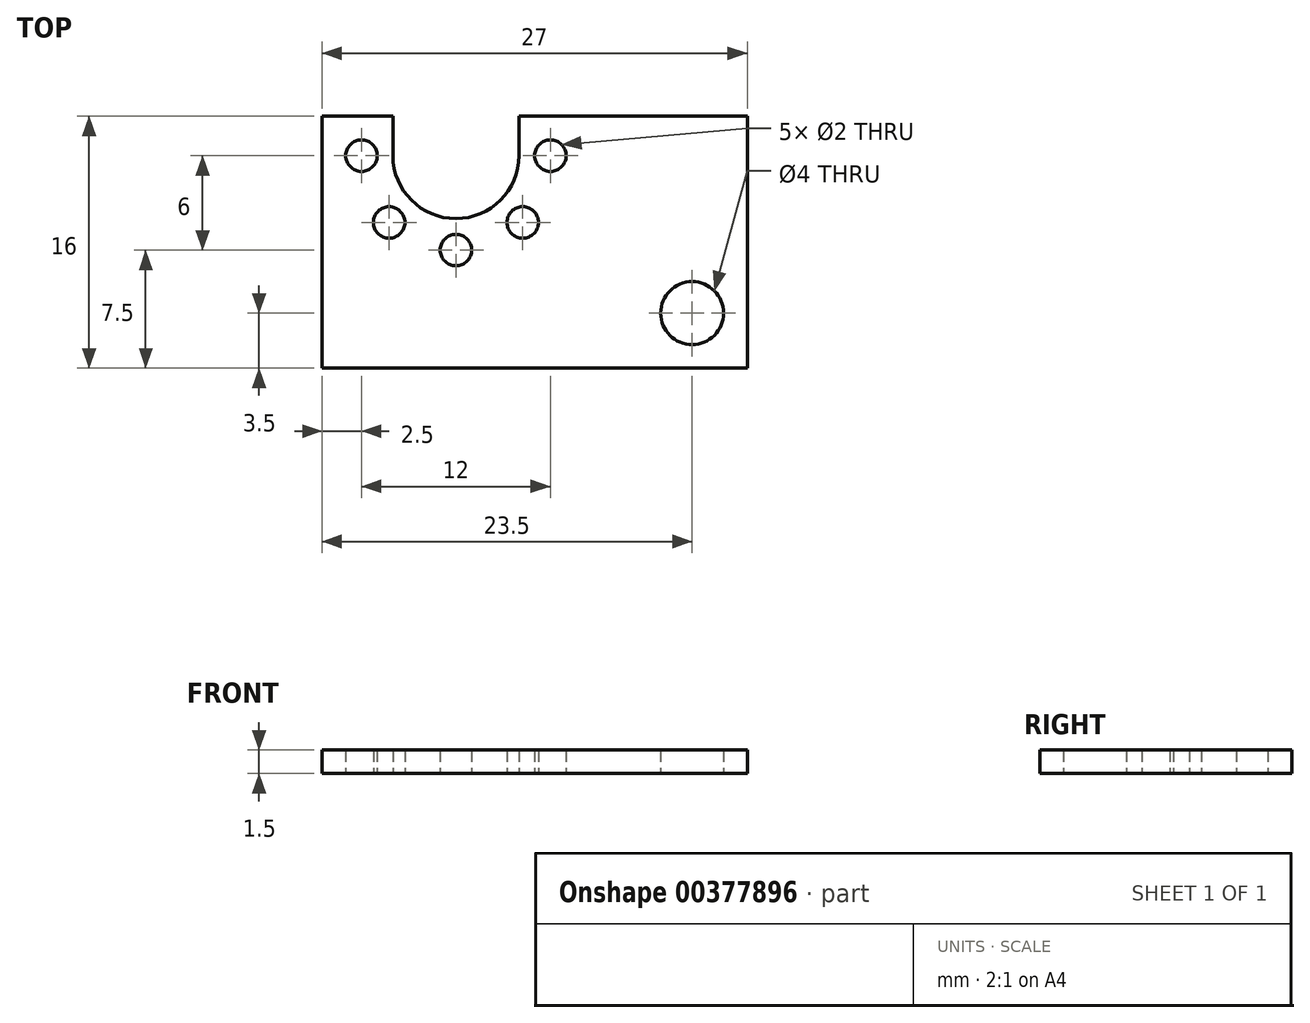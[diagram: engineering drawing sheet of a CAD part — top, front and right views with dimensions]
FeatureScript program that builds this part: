
annotation { "Feature Type Name" : "Feature", "Feature Type Description" : "" }
export const myFeature = defineFeature(function(context is Context, id is Id, definition is map)
    precondition{}
    {
        {
            var Q0;
            Q0=qCreatedBy(makeId("Top.planeOp"),FACE);
            var sketch = newSketch(context, id + "F0", { "sketchPlane" : qUnion([Q0])});
            skArc(sketch, "E0", {"start": v(-4, 0) * mm, "mid": v(0, -4) * mm, "end": v(4, 0) * mm});
            skCircle(sketch, "E1", {"center": v(6, 0) * mm, "radius": 1 * mm});
            skCircle(sketch, "E2.4.0", {"center": v(-6, 0) * mm, "radius": 1 * mm});
            skCircle(sketch, "E2.5.0", {"center": v(-4.24, -4.24) * mm, "radius": 1 * mm});
            skCircle(sketch, "E2.6.0", {"center": v(0, -6) * mm, "radius": 1 * mm});
            skCircle(sketch, "E2.7.0", {"center": v(4.24, -4.24) * mm, "radius": 1 * mm});
            skLineSegment(sketch, "E3.bottom", {"start": v(-8.5, 2.5) * mm, "end": v(-4, 2.5) * mm});
            skLineSegment(sketch, "E3.top", {"start": v(-8.5, -13.5) * mm, "end": v(18.5, -13.5) * mm});
            skLineSegment(sketch, "E3.left", {"start": v(-8.5, 2.5) * mm, "end": v(-8.5, -13.5) * mm});
            skLineSegment(sketch, "E3.right", {"start": v(18.5, 2.5) * mm, "end": v(18.5, -13.5) * mm});
            skLineSegment(sketch, "E4", {"start": v(-4, 0) * mm, "end": v(-4, 2.5) * mm});
            skLineSegment(sketch, "E5.MirrorCS", {"start": v(4, 0) * mm, "end": v(4, 2.5) * mm});
            skLineSegment(sketch, "E6.trimOffspring", {"start": v(4, 2.5) * mm, "end": v(18.5, 2.5) * mm});
            skCircle(sketch, "E7", {"center": v(15, -10) * mm, "radius": 2 * mm});
            skSolve(sketch);
        }
        {
            var Q0;
            Q0 = qSketchRegion(id + "F0", true);
            extrude(context, id + "F1", {"entities" : qUnion([Q0]), "depth" : 1.5 * mm});
        }
    });
